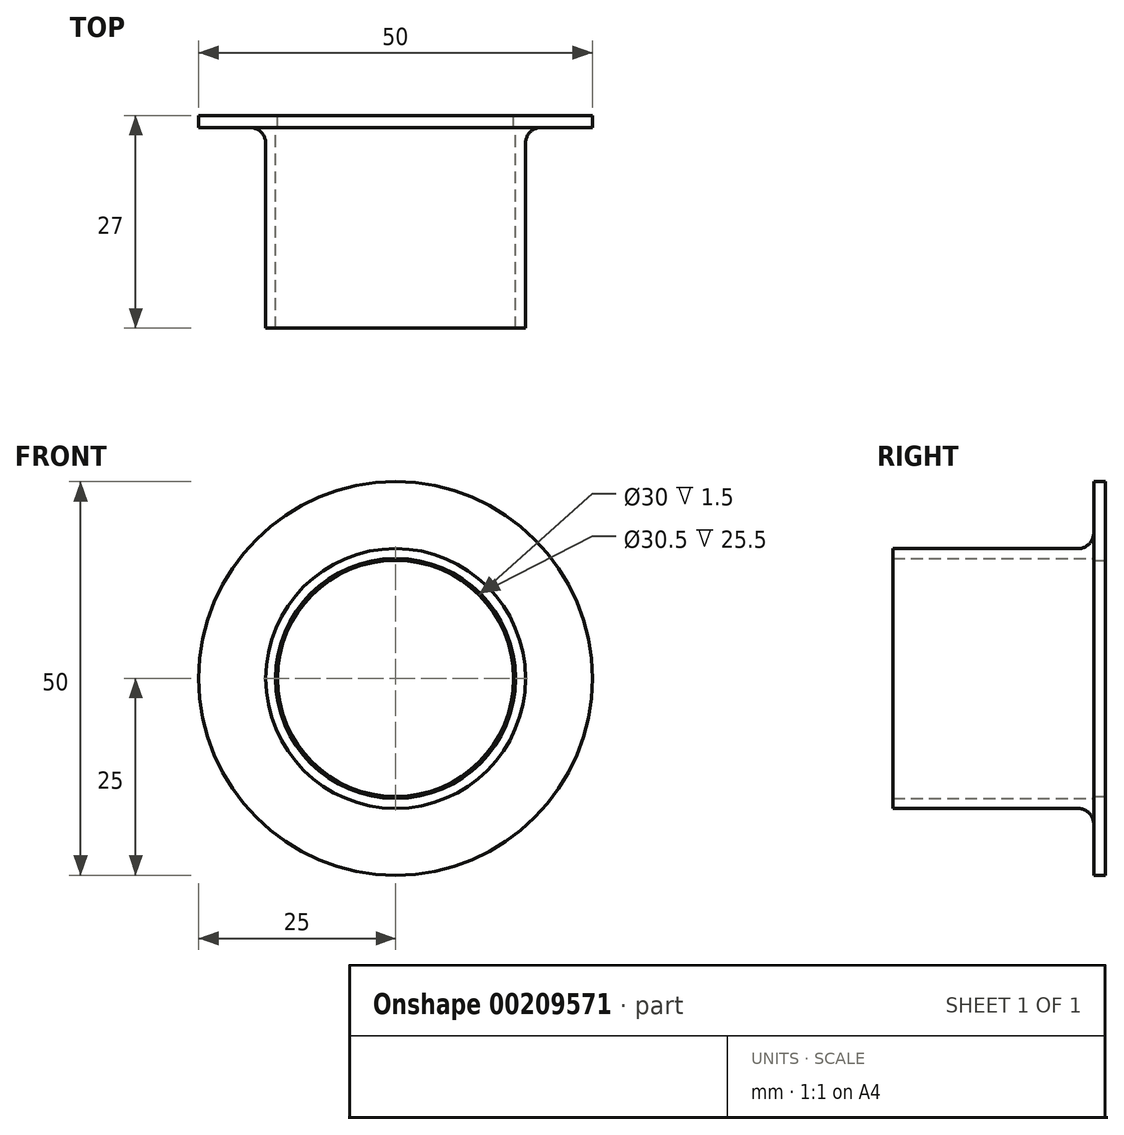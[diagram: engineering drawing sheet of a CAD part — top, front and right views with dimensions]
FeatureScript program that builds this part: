
annotation { "Feature Type Name" : "Feature", "Feature Type Description" : "" }
export const myFeature = defineFeature(function(context is Context, id is Id, definition is map)
    precondition{}
    {
        {
            var Q0;
            Q0=qCreatedBy(makeId("Front.planeOp"),FACE);
            var sketch = newSketch(context, id + "F0", { "sketchPlane" : qUnion([Q0])});
            skCircle(sketch, "E0", {"center": v(0, 0) * mm, "radius": 15 * mm});
            skCircle(sketch, "E1", {"center": v(0, 0) * mm, "radius": 25 * mm});
            skSolve(sketch);
        }
        {
            var Q0;
            Q0=makeQuery(id+"F0.imprint","IMPRINT",FACE,{"disambiguationData":[TD([[makeQuery(id+"F0.imprint","IMPRINT",EDGE,{"derivedFrom":sQuery(id+"F0.wireOp",EDGE,"E0")}),-1.0]])]});
            extrude(context, id + "F1", {"entities" : qUnion([Q0]), "depth" : 1.5 * mm});
        }
        {
            var Q0;
            Q0=qCreatedBy(makeId("Front.planeOp"),FACE);
            var sketch = newSketch(context, id + "F2", { "sketchPlane" : qUnion([Q0])});
            skCircle(sketch, "E2", {"center": v(0, 0) * mm, "radius": 16.5 * mm});
            skCircle(sketch, "E3", {"center": v(0, 0) * mm, "radius": 15.25 * mm});
            skSolve(sketch);
        }
        {
            var Q0;
            Q0=makeQuery(id+"F2.imprint","IMPRINT",FACE,{"disambiguationData":[TD([[makeQuery(id+"F2.imprint","IMPRINT",EDGE,{"derivedFrom":sQuery(id+"F2.wireOp",EDGE,"E2")}),1.0]])]});
            extrude(context, id + "F3", {"entities" : qUnion([Q0]), "operationType" : NewBodyOperationType.ADD, "depth" : 27 * mm});
        }
        {
            var Q0;
            Q0=makeQuery(id+"F3.boolean.opBoolean","INTERSECT",EDGE,{"derivedFrom":[makeQuery(id+"F1.opExtrude","CAP_FACE",FACE,{"disambiguationData":[OSD([sQuery(id+"F0.wireOp",EDGE,"E0"),sQuery(id+"F0.wireOp",EDGE,"E1")])],"isStart":false}),makeQuery(id+"F3.opExtrude","SWEPT_FACE",FACE,{"disambiguationData":[OSD([sQuery(id+"F2.wireOp",EDGE,"E2")])]})]});
            fillet(context, id + "F4", {"entities" : qUnion([Q0]), "radius" : 2 * mm, "tangentPropagation" : true, "allowEdgeOverflow" : false});
        }
    });
